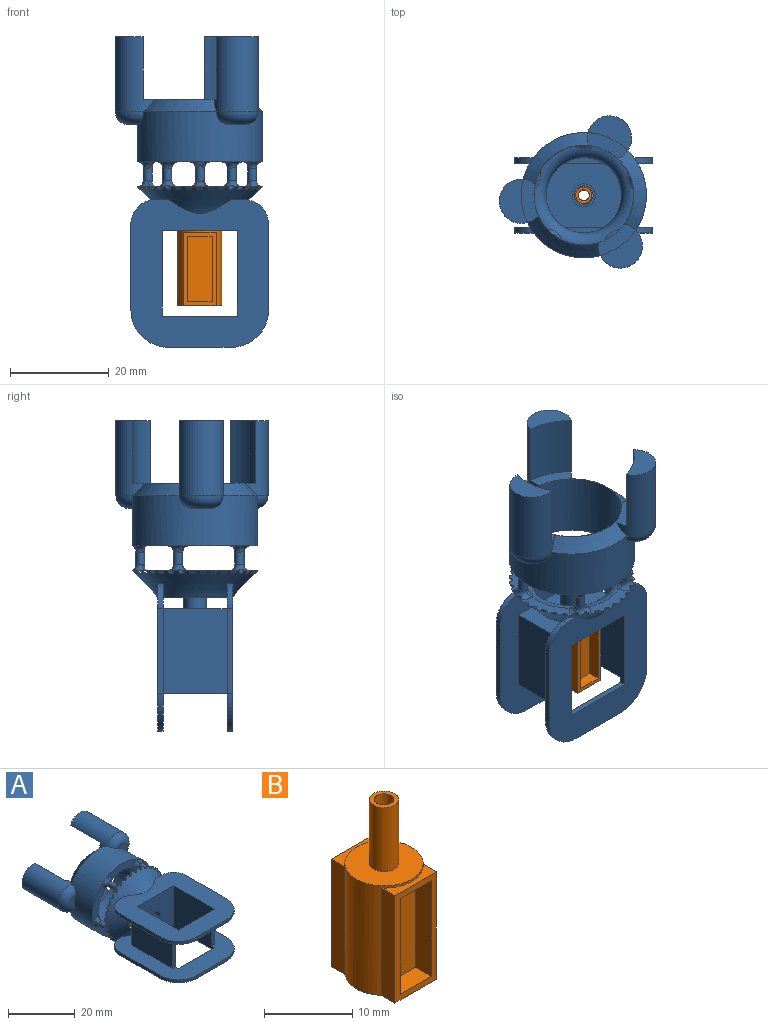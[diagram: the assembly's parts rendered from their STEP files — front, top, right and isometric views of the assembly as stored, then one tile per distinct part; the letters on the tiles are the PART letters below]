
ASSEMBLY  parts=2 mates=1
PART A: 162 faces, bbox 31.4x63.3x31.2 mm
  f0: plane 15.24x1.13mm, normal (0,1,0), area 17.3mm2, adj f1,f2,f139,f144
  f1: plane 17.27x15.24mm, normal (-1,0,0), area 246.7mm2, adj f0,f138,f139,f140,f141,f142,f144,f156
  f2: plane 17.27x15.24mm, normal (1,0,0), area 246.7mm2, adj f0,f138,f139,f140,f141,f142,f144,f157
  f3: cylinder r=7.62mm len=12.97mm, axis (0,1,0), area 44.5mm2, adj f5,f71,f142,f144
  f4: cylinder r=7.62mm len=12.97mm, axis (0,1,0), area 44.5mm2, adj f5,f71,f142,f144
  f5: revolved ~25.29x25.29mm, area 410.1mm2, adj f3,f4,f6,f7,f8,f9,f10,f12
  f6: cylinder r=0.62mm len=1.22mm, axis (0,1,0), area 0mm2, adj f5,f60
  f7: cylinder r=0.62mm len=1.24mm, axis (0,1,0), area 0mm2, adj f5,f60
  f8: cylinder r=0.62mm len=1.22mm, axis (0,1,0), area 0mm2, adj f5,f60
  f9: cylinder r=0.62mm len=1.18mm, axis (0,1,0), area 0mm2, adj f5,f60
  f10: cylinder r=0.62mm len=1.15mm, axis (0,1,0), area 0.9mm2, adj f5,f11,f60,f90,f123
  f11: cylinder r=12.7mm len=0.84mm, axis (0,1,0), area 0.1mm2, adj f10,f12,f90,f123
  f12: cylinder r=0.62mm len=1.04mm, axis (0,1,0), area 1mm2, adj f5,f11,f61,f90,f123
  f13: cylinder r=0.62mm len=1.06mm, axis (0,1,0), area 0mm2, adj f5,f61
  f14: cylinder r=0.62mm len=1.13mm, axis (0,1,0), area 0mm2, adj f5,f61
  f15: cylinder r=0.62mm len=1.19mm, axis (0,1,0), area 0mm2, adj f5,f61
  f16: cylinder r=0.62mm len=1.23mm, axis (0,1,0), area 0mm2, adj f5,f61
  f17: cylinder r=0.62mm len=1.24mm, axis (0,1,0), area 0mm2, adj f5,f61
  f18: cylinder r=0.62mm len=1.23mm, axis (0,1,0), area 0.9mm2, adj f5,f19,f61,f92,f124
  f19: cylinder r=12.7mm len=0.98mm, axis (0,1,0), area 0.1mm2, adj f18,f20,f92,f124
  f20: cylinder r=0.62mm len=1.16mm, axis (0,1,0), area 1mm2, adj f5,f19,f62,f92,f124
  f21: cylinder r=0.62mm len=1.1mm, axis (0,1,0), area 0mm2, adj f5,f62
  f22: cylinder r=0.62mm len=1.02mm, axis (0,1,0), area 0mm2, adj f5,f62
  f23: cylinder r=0.62mm len=1.08mm, axis (0,1,0), area 0mm2, adj f5,f62
  f24: cylinder r=0.62mm len=1.15mm, axis (0,1,0), area 0mm2, adj f5,f62
  f25: cylinder r=0.62mm len=1.2mm, axis (0,1,0), area 0mm2, adj f5,f62
  f26: cylinder r=0.62mm len=1.23mm, axis (0,1,0), area 0.9mm2, adj f5,f27,f62,f94,f125
  f27: cylinder r=12.7mm len=1.04mm, axis (0,1,0), area 0.1mm2, adj f26,f28,f94,f125
  f28: cylinder r=0.62mm len=1.23mm, axis (0,1,0), area 1mm2, adj f5,f27,f63,f94,f125
  f29: cylinder r=0.62mm len=1.2mm, axis (0,1,0), area 0mm2, adj f5,f63
  f30: cylinder r=0.62mm len=1.15mm, axis (0,1,0), area 0mm2, adj f5,f63
  f31: cylinder r=0.62mm len=1.08mm, axis (0,1,0), area 0mm2, adj f5,f63
  f32: cylinder r=0.62mm len=1.02mm, axis (0,1,0), area 0mm2, adj f5,f63
  f33: cylinder r=0.62mm len=1.1mm, axis (0,1,0), area 0mm2, adj f5,f63
  f34: cylinder r=0.62mm len=1.16mm, axis (0,1,0), area 0.9mm2, adj f5,f35,f63,f96,f126
  f35: cylinder r=12.7mm len=0.98mm, axis (0,1,0), area 0.1mm2, adj f34,f36,f96,f126
  f36: cylinder r=0.62mm len=1.23mm, axis (0,1,0), area 1mm2, adj f5,f35,f65,f96,f126
  f37: cylinder r=0.62mm len=1.24mm, axis (0,1,0), area 0mm2, adj f5,f65
  f38: cylinder r=0.62mm len=1.23mm, axis (0,1,0), area 0mm2, adj f5,f65
  f39: cylinder r=0.62mm len=1.19mm, axis (0,1,0), area 0mm2, adj f5,f65
  f40: cylinder r=0.62mm len=1.13mm, axis (0,1,0), area 0mm2, adj f5,f65
  f41: cylinder r=0.62mm len=1.06mm, axis (0,1,0), area 0mm2, adj f5,f65
  f42: cylinder r=0.62mm len=1.04mm, axis (0,1,0), area 0.9mm2, adj f5,f43,f65,f98,f127
  f43: cylinder r=12.7mm len=0.84mm, axis (0,1,0), area 0.1mm2, adj f42,f44,f98,f127
  f44: cylinder r=0.62mm len=1.15mm, axis (0,1,0), area 1mm2, adj f5,f43,f60,f98,f127
  f45: cylinder r=0.62mm len=1.18mm, axis (0,1,0), area 0mm2, adj f5,f60
  f46: bspline ~1.52x1.11mm, area 1mm2, adj f47,f66,f72,f116
  f47: bspline ~1.4x1.27mm, area 0.7mm2, adj f46,f66,f72,f117
  f48: bspline ~1.87x0.88mm, area 1mm2, adj f49,f68,f72,f115
  f49: bspline ~1.45x1.27mm, area 0.7mm2, adj f48,f68,f72,f114
  f50: bspline ~1.78x0.88mm, area 1mm2, adj f51,f67,f72,f108
  f51: bspline ~1.49x1.27mm, area 0.7mm2, adj f50,f67,f72,f109
  f52: bspline ~1.51x1.13mm, area 1mm2, adj f53,f70,f72,f104
  f53: bspline ~1.27x1.19mm, area 0.7mm2, adj f52,f70,f72,f105
  f54: bspline ~1.77x0.88mm, area 1mm2, adj f55,f69,f72,f103
  f55: bspline ~1.27x1.26mm, area 0.7mm2, adj f54,f69,f72,f102
  f56: plane 9.96x7.78mm, normal (0,-1,0), area 26.8mm2, adj f64,f72,f102,f113
  f57: plane 12.26x3.63mm, normal (0,-1,0), area 26.8mm2, adj f64,f72,f106,f117
  f58: plane 9.88x7.86mm, normal (0,-1,0), area 26.8mm2, adj f64,f72,f110,f114
  f59: plane 11.64x5.44mm, normal (0,-1,0), area 26.8mm2, adj f64,f72,f109,f118
  f60: plane 11.89x3.49mm, normal (0,1,0), area 22.8mm2, adj f5,f6,f7,f8,f9,f10,f44,f45
  f61: plane 11.31x5.25mm, normal (0,1,0), area 22.8mm2, adj f5,f12,f13,f14,f15,f16,f17,f18
  f62: plane 9.67x7.64mm, normal (0,1,0), area 22.8mm2, adj f5,f20,f21,f22,f23,f24,f25,f26
  f63: plane 9.63x7.73mm, normal (0,1,0), area 22.8mm2, adj f5,f28,f29,f30,f31,f32,f33,f34
  f64: cylinder r=12.7mm len=25.4mm, axis (0,-1,0), area 750.5mm2, adj f56,f57,f58,f59,f74,f77,f81,f85
  f65: plane 11.31x5.32mm, normal (0,1,0), area 22.8mm2, adj f5,f36,f37,f38,f39,f40,f41,f42
  f66: cylinder r=0.89mm len=3.36mm, axis (0,-1,0), area 14.9mm2, adj f46,f47,f98,f99,f116,f117,f118,f119
  f67: cylinder r=0.89mm len=2.93mm, axis (0,-1,0), area 14.7mm2, adj f50,f51,f96,f97,f108,f109,f110,f111
  f68: cylinder r=0.89mm len=2.93mm, axis (0,-1,0), area 14.7mm2, adj f48,f49,f94,f95,f112,f113,f114,f115
  f69: cylinder r=0.89mm len=2.93mm, axis (0,-1,0), area 14.7mm2, adj f54,f55,f92,f93,f100,f101,f102,f103
  f70: cylinder r=0.89mm len=3.35mm, axis (0,-1,0), area 14.9mm2, adj f52,f53,f90,f91,f104,f105,f106,f107
  f71: torus R=10.16mm, axis (0,-1,0), area 203.6mm2, adj f3,f4,f60,f61,f62,f63,f65,f91
  f72: cylinder r=10.1mm len=20.19mm, axis (0,-1,0), area 805.7mm2, adj f46,f47,f48,f49,f50,f51,f52,f53
  f73: plane 24.92x23.23mm, normal (0,1,0), area 65.6mm2, adj f72,f75,f76,f79,f80,f83,f84,f120
  f74: plane 11.68x5.37mm, normal (0,-1,0), area 26.8mm2, adj f64,f72,f101,f105
  f75: cylinder r=12.7mm len=12.7mm, axis (0,1,0), area 114.5mm2, adj f73,f76,f78
  f76: cylinder r=4.48mm len=15.24mm, axis (0,1,0), area 245.4mm2, adj f73,f75,f78,f88,f120,f122
  f77: plane 3.6x3.19mm, normal (0,-1,0), area 6.1mm2, adj f64,f88
  f78: plane 8.53x7.7mm, normal (0,1,0), area 33.9mm2, adj f75,f76
  f79: cylinder r=12.7mm len=12.7mm, axis (0,1,0), area 114.5mm2, adj f73,f80,f82
  f80: cylinder r=4.48mm len=15.24mm, axis (0,1,0), area 245.4mm2, adj f73,f79,f82,f89,f120,f121
  f81: plane 3.77x2.88mm, normal (0,-1,0), area 6.1mm2, adj f64,f89
  f82: plane 8.83x7.02mm, normal (0,1,0), area 33.9mm2, adj f79,f80
  f83: cylinder r=12.7mm len=12.7mm, axis (0,1,0), area 114.5mm2, adj f73,f84,f86
  f84: cylinder r=4.48mm len=15.24mm, axis (0,1,0), area 245.4mm2, adj f73,f83,f86,f87,f121,f122
  f85: plane 3.88x2.28mm, normal (0,-1,0), area 6.1mm2, adj f64,f87
  f86: plane 8.97x5.71mm, normal (0,1,0), area 33.9mm2, adj f83,f84
  f87: torus R=1.94mm, axis (0,1,0), area 48.4mm2, adj f64,f84,f85
  f88: torus R=1.94mm, axis (0,1,0), area 48.4mm2, adj f64,f76,f77
  f89: torus R=1.94mm, axis (0,1,0), area 48.4mm2, adj f64,f80,f81
  f90: torus R=2.16mm, axis (0,-1,0), area 8.8mm2, adj f10,f11,f12,f60,f61,f70,f91
  f91: bspline ~3.25x2.51mm, area 4.5mm2, adj f70,f71,f90
  f92: torus R=2.16mm, axis (0,-1,0), area 8.8mm2, adj f18,f19,f20,f61,f62,f69,f93
  f93: bspline ~3.63x1.83mm, area 4.5mm2, adj f69,f71,f92
  f94: torus R=2.16mm, axis (0,-1,0), area 8.8mm2, adj f26,f27,f28,f62,f63,f68,f95
  f95: bspline ~4x1.46mm, area 4.5mm2, adj f68,f71,f94
  f96: torus R=2.16mm, axis (0,-1,0), area 8.8mm2, adj f34,f35,f36,f63,f65,f67,f97
  f97: bspline ~3.76x1.69mm, area 4.5mm2, adj f67,f71,f96
  f98: torus R=2.16mm, axis (0,-1,0), area 8.8mm2, adj f42,f43,f44,f60,f65,f66,f99
  f99: bspline ~3.27x2.48mm, area 4.5mm2, adj f66,f71,f98
  f100: bspline ~3.38x1.66mm, area 3.1mm2, adj f64,f69,f101,f102
  f101: torus R=2.16mm, axis (0,1,0), area 3.6mm2, adj f69,f74,f100,f103
  f102: torus R=2.16mm, axis (0,1,0), area 3.6mm2, adj f55,f56,f69,f100
  f103: bspline ~1.5x1.27mm, area 0.7mm2, adj f54,f69,f72,f101
  f104: bspline ~1.39x1.27mm, area 0.7mm2, adj f52,f70,f72,f106
  f105: torus R=2.16mm, axis (0,1,0), area 3.6mm2, adj f53,f70,f74,f107
  f106: torus R=2.16mm, axis (0,1,0), area 3.6mm2, adj f57,f70,f104,f107
  f107: bspline ~2.87x2.23mm, area 3.1mm2, adj f64,f70,f105,f106
  f108: bspline ~1.27x1.27mm, area 0.7mm2, adj f50,f67,f72,f110
  f109: torus R=2.16mm, axis (0,1,0), area 3.6mm2, adj f51,f59,f67,f111
  f110: torus R=2.16mm, axis (0,1,0), area 3.6mm2, adj f58,f67,f108,f111
  f111: bspline ~3.39x1.65mm, area 3.1mm2, adj f64,f67,f109,f110
  f112: bspline ~3.56x1.42mm, area 3.1mm2, adj f64,f68,f113,f114
  f113: torus R=2.16mm, axis (0,1,0), area 3.6mm2, adj f56,f68,f112,f115
  f114: torus R=2.16mm, axis (0,1,0), area 3.6mm2, adj f49,f58,f68,f112
  f115: bspline ~1.45x1.27mm, area 0.7mm2, adj f48,f68,f72,f113
  f116: bspline ~1.27x1.19mm, area 0.7mm2, adj f46,f66,f72,f118
  f117: torus R=2.16mm, axis (0,1,0), area 3.6mm2, adj f47,f57,f66,f119
  f118: torus R=2.16mm, axis (0,1,0), area 3.6mm2, adj f59,f66,f116,f119
  f119: bspline ~2.89x2.21mm, area 3.1mm2, adj f64,f66,f117,f118
  f120: cone r=10.16mm half-angle=45deg, axis (0,-1,0), area 57mm2, adj f64,f73,f76,f80
  f121: cone r=10.16mm half-angle=45deg, axis (0,-1,0), area 57mm2, adj f64,f73,f80,f84
  f122: cone r=10.16mm half-angle=45deg, axis (0,-1,0), area 57mm2, adj f64,f73,f76,f84
  f123: plane 0.87x0.65mm, normal (0,-1,0), area 0.1mm2, adj f5,f10,f11,f12
  f124: plane 1x0.37mm, normal (0,-1,0), area 0.1mm2, adj f5,f18,f19,f20
  f125: plane 1.04x0.07mm, normal (0,-1,0), area 0.1mm2, adj f5,f26,f27,f28
  f126: plane 1x0.37mm, normal (0,-1,0), area 0.1mm2, adj f5,f34,f35,f36
  f127: plane 0.87x0.65mm, normal (0,-1,0), area 0.1mm2, adj f5,f42,f43,f44
  f128: plane 8x1.13mm, normal (0,1,0), area 6.1mm2, adj f71,f144
  f129: plane 2.46x1.13mm, normal (0,1,0), area 2.1mm2, adj f5,f139,f144,f155
  f130: plane 8x1.13mm, normal (0,1,0), area 6.1mm2, adj f71,f142
  f131: plane 2.46x1.13mm, normal (0,1,0), area 2.1mm2, adj f5,f138,f142,f153
  f132: plane 17.78x12.97mm, normal (0,1,0), area 213.5mm2, adj f133,f134,f136,f142,f144
  f133: plane 17.27x12.97mm, normal (1,0,0), area 224.1mm2, adj f132,f142,f144,f156
  f134: plane 17.27x12.97mm, normal (-1,0,0), area 224.1mm2, adj f132,f142,f144,f157
  f135: cylinder r=1.91mm len=8.89mm, axis (0,1,0), area 106.4mm2, adj f137,f141
  f136: cylinder r=2.34mm len=7.62mm, axis (0,1,0), area 112.1mm2, adj f132,f137
  f137: plane 4.68x4.68mm, normal (0,1,0), area 5.8mm2, adj f135,f136
  f138: plane 29.97x27.94mm, normal (0,0,-1), area 515.5mm2, adj f1,f2,f5,f131,f140,f141,f143,f147
  f139: plane 29.97x27.94mm, normal (0,0,1), area 515.5mm2, adj f0,f1,f2,f5,f129,f141,f145,f146
  f140: plane 15.24x1.13mm, normal (0,1,0), area 17.3mm2, adj f1,f2,f138,f142
  f141: plane 15.24x15.24mm, normal (0,-1,0), area 220.9mm2, adj f1,f2,f135,f138,f139
  f142: plane 30.33x28.29mm, normal (0,0,1), area 464.9mm2, adj f1,f2,f3,f4,f5,f130,f131,f132
  f143: plane 17.27x1.13mm, normal (-1,0,0), area 19.6mm2, adj f138,f142,f153,f160
  f144: plane 30.33x28.29mm, normal (0,0,-1), area 464.9mm2, adj f0,f1,f2,f3,f4,f5,f128,f129
  f145: plane 17.27x1.13mm, normal (-1,0,0), area 19.6mm2, adj f139,f144,f154,f159
  f146: plane 17.27x1.13mm, normal (1,0,0), area 19.6mm2, adj f139,f144,f155,f158
  f147: plane 17.27x1.13mm, normal (1,0,0), area 19.6mm2, adj f138,f142,f152,f161
  f148: plane 12.7x1.13mm, normal (0,-1,0), area 14.4mm2, adj f138,f142,f160,f161
  f149: plane 12.7x1.13mm, normal (0,-1,0), area 14.4mm2, adj f139,f144,f158,f159
  f150: plane 2.46x1.13mm, normal (0,1,0), area 2.1mm2, adj f5,f139,f144,f154
  f151: plane 2.46x1.13mm, normal (0,1,0), area 2.1mm2, adj f5,f138,f142,f152
  f152: cylinder r=5.08mm len=5.08mm, axis (0,0,-1), area 9mm2, adj f138,f142,f147,f151
  f153: cylinder r=5.08mm len=5.08mm, axis (0,0,-1), area 9mm2, adj f131,f138,f142,f143
  f154: cylinder r=5.08mm len=5.08mm, axis (0,0,-1), area 9mm2, adj f139,f144,f145,f150
  f155: cylinder r=5.08mm len=5.08mm, axis (0,0,-1), area 9mm2, adj f129,f139,f144,f146
  f156: plane 12.97x1.27mm, normal (0,-1,0), area 16.5mm2, adj f1,f133,f142,f144
  f157: plane 12.97x1.27mm, normal (0,-1,0), area 16.5mm2, adj f2,f134,f142,f144
  f158: cylinder r=7.62mm len=7.62mm, axis (0,0,-1), area 13.6mm2, adj f139,f144,f146,f149
  f159: cylinder r=7.62mm len=7.62mm, axis (0,0,-1), area 13.6mm2, adj f139,f144,f145,f149
  f160: cylinder r=7.62mm len=7.62mm, axis (0,0,-1), area 13.6mm2, adj f138,f142,f143,f148
  f161: cylinder r=7.62mm len=7.62mm, axis (0,0,-1), area 13.6mm2, adj f138,f142,f147,f148
PART B: 24 faces, bbox 8.9x10.2x24.1 mm
  f0: cylinder r=4.45mm len=15.24mm, axis (0,0,-1), area 201.9mm2, adj f1,f2,f8,f9,f10,f12,f13,f18
  f1: plane 8.89x8.89mm, normal (0,0,1), area 53.5mm2, adj f0,f22
  f2: plane 10.16x8.89mm, normal (0,0,-1), area 72.8mm2, adj f0,f7,f8,f9,f11,f12,f13,f21
  f3: plane 5x2.54mm, normal (0,0,1), area 12.7mm2, adj f4,f6,f7,f19
  f4: plane 13.3x2.54mm, normal (-1,0,0), area 33.8mm2, adj f3,f5,f7,f19
  f5: plane 5x2.54mm, normal (0,0,-1), area 12.7mm2, adj f4,f6,f7,f19
  f6: plane 13.3x2.54mm, normal (1,0,0), area 33.8mm2, adj f3,f5,f7,f19
  f7: plane 14.93x6.64mm, normal (0,-1,0), area 32.6mm2, adj f2,f3,f4,f5,f6,f8,f9,f10
  f8: plane 14.93x2.12mm, normal (-1,0,0), area 31.7mm2, adj f0,f2,f7,f10
  f9: plane 14.93x2.12mm, normal (1,0,0), area 31.7mm2, adj f0,f2,f7,f10
  f10: plane 6.64x2.12mm, normal (0,0,1), area 7.2mm2, adj f0,f7,f8,f9
  f11: plane 14.93x6.64mm, normal (0,1,0), area 32.6mm2, adj f2,f12,f13,f14,f15,f16,f17,f18
  f12: plane 14.93x2.12mm, normal (1,0,0), area 31.7mm2, adj f0,f2,f11,f18
  f13: plane 14.93x2.12mm, normal (-1,0,0), area 31.7mm2, adj f0,f2,f11,f18
  f14: plane 5x2.54mm, normal (0,0,1), area 12.7mm2, adj f11,f15,f17,f20
  f15: plane 13.3x2.54mm, normal (-1,0,0), area 33.8mm2, adj f11,f14,f16,f20
  f16: plane 5x2.54mm, normal (0,0,-1), area 12.7mm2, adj f11,f15,f17,f20
  f17: plane 13.3x2.54mm, normal (1,0,0), area 33.8mm2, adj f11,f14,f16,f20
  f18: plane 6.64x2.12mm, normal (0,0,1), area 7.2mm2, adj f0,f11,f12,f13
  f19: plane 13.3x5mm, normal (0,-1,0), area 66.5mm2, adj f3,f4,f5,f6
  f20: plane 13.3x5mm, normal (0,1,0), area 66.5mm2, adj f14,f15,f16,f17
  f21: cylinder r=1.1mm len=24.13mm, axis (0,0,-1), area 166.8mm2, adj f2,f23
  f22: cylinder r=1.65mm len=8.89mm, axis (0,0,-1), area 92.2mm2, adj f1,f23
  f23: plane 3.3x3.3mm, normal (0,0,1), area 4.8mm2, adj f21,f22
PLACE A rot(axis=(1,0,0),90deg) t=(-2.18,9.19,24.34)mm
PLACE B t=(-2.18,9.19,0.21)mm
MATE revolute A.f135 <-> B.f22  axis (0,0,-1) through (-2.18,9.19,15.45)mm
